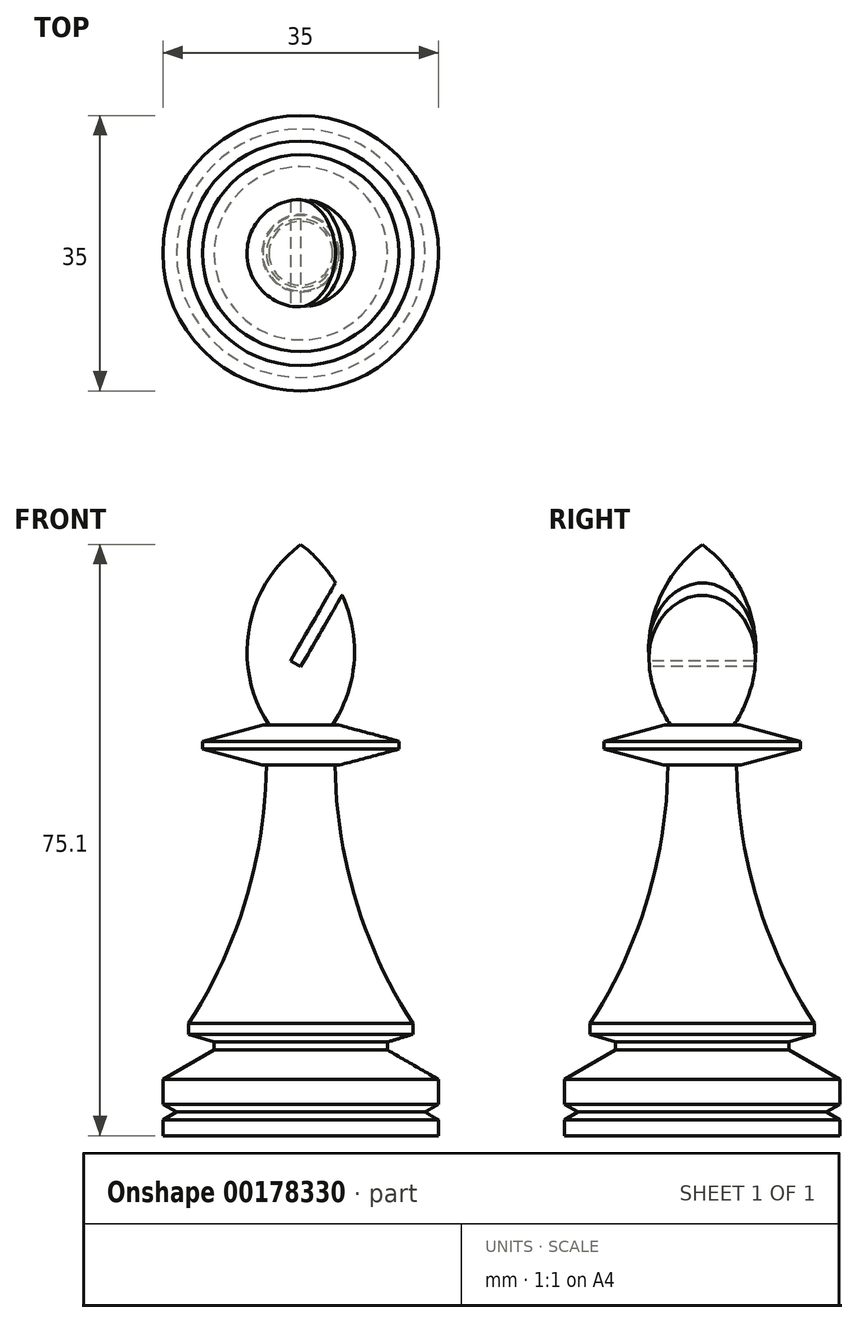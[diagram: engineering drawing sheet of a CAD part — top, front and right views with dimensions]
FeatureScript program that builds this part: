
annotation { "Feature Type Name" : "Feature", "Feature Type Description" : "" }
export const myFeature = defineFeature(function(context is Context, id is Id, definition is map)
    precondition{}
    {
        {
            var Q0;
            Q0=qCreatedBy(makeId("Front.planeOp"),FACE);
            var sketch = newSketch(context, id + "F0", { "sketchPlane" : qUnion([Q0])});
            skLineSegment(sketch, "E0", {"start": v(0, 0) * mm, "end": v(17.5, 0) * mm});
            skLineSegment(sketch, "E1", {"start": v(17.5, 0) * mm, "end": v(17.5, 2) * mm});
            skLineSegment(sketch, "E2", {"start": v(17.5, 7.13) * mm, "end": v(11, 10.89) * mm});
            skLineSegment(sketch, "E3", {"start": v(0, 14.4) * mm, "end": v(0, 0) * mm});
            skPoint(sketch, "E4.endSnap0", {"position": v(17.5, 3.57) * mm});
            skLineSegment(sketch, "E5", {"start": v(17.5, 2) * mm, "end": v(15.77, 3) * mm});
            skLineSegment(sketch, "E6", {"start": v(15.77, 3) * mm, "end": v(17.5, 4) * mm});
            skLineSegment(sketch, "E7.trimOffspring", {"start": v(17.5, 3.57) * mm, "end": v(17.5, 7.13) * mm});
            skLineSegment(sketch, "E8", {"start": v(11, 10.89) * mm, "end": v(11, 11.89) * mm});
            skLineSegment(sketch, "E9", {"start": v(11, 11.89) * mm, "end": v(14.25, 12.89) * mm});
            skLineSegment(sketch, "E10", {"start": v(14.25, 14.25) * mm, "end": v(14.25, 12.89) * mm});
            skLineSegment(sketch, "E11", {"start": v(0, 0) * mm, "end": v(0, 78) * mm});
            skArc(sketch, "E12", {"start": v(2.57, 74.16) * mm, "mid": v(1.37, 74.86) * mm, "end": v(0, 75.1) * mm});
            skPoint(sketch, "E13.first.point", {"position": v(2.57, 74.16) * mm});
            skPoint(sketch, "E13.third.point", {"position": v(10.83, 51.5) * mm});
            skLineSegment(sketch, "E14", {"start": v(12.5, 50.1) * mm, "end": v(12.5, 49.1) * mm});
            skLineSegment(sketch, "E15", {"start": v(12.5, 50.1) * mm, "end": v(4.8, 52.17) * mm});
            skLineSegment(sketch, "E16", {"start": v(12.5, 49.1) * mm, "end": v(4.92, 47.08) * mm});
            skLineSegment(sketch, "E17", {"start": v(4.05, 52.17) * mm, "end": v(4.8, 52.17) * mm});
            skArc(sketch, "E18", {"start": v(4.36, 47.09) * mm, "mid": v(6.97, 29.97) * mm, "end": v(14.25, 14.25) * mm});
            skPoint(sketch, "E18.first.point", {"position": v(4.36, 47.09) * mm});
            skPoint(sketch, "E18.second.point", {"position": v(75.46, -13.1) * mm});
            skPoint(sketch, "E18.third.point", {"position": v(14.25, 14.25) * mm});
            skPoint(sketch, "E19.orphan", {"position": v(0, 49.17) * mm});
            skPoint(sketch, "E20.start.orphan", {"position": v(0, 50.17) * mm});
            skLineSegment(sketch, "E21", {"start": v(0, 52.17) * mm, "end": v(0, 47.17) * mm});
            skLineSegment(sketch, "E22", {"start": v(4.92, 47.08) * mm, "end": v(4.36, 47.09) * mm});
            skArc(sketch, "E23", {"start": v(4.05, 52.17) * mm, "mid": v(6.57, 64.44) * mm, "end": v(0, 75.1) * mm});
            skPoint(sketch, "E23.second.point", {"position": v(-21.42, 48.8) * mm});
            skPoint(sketch, "E23.third.point", {"position": v(6.42, 65.18) * mm});
            skLineSegment(sketch, "E24", {"start": v(0, 75.1) * mm, "end": v(0, 0) * mm});
            skSolve(sketch);
        }
        {
            var Q0;
            {var subQ1=sQuery(id+"F0.wireOp",EDGE,"E0");Q0=makeQuery(id+"F0.imprint","IMPRINT",FACE,{"disambiguationData":[TD([[makeQuery(id+"F0.imprint","IMPRINT",EDGE,{"derivedFrom":subQ1}),1.0]])]});}
            var Q1;
            Q1=sQuery(id+"F0.wireOp",EDGE,"E3");
            revolve(context, id + "F1", {"entities" : qUnion([Q0]), "axis" : qUnion([Q1]), "revolveType" : RevolveType.FULL});
        }
        {
            var Q0;
            Q0=qCreatedBy(makeId("Front.planeOp"),FACE);
            var sketch = newSketch(context, id + "F2", { "sketchPlane" : qUnion([Q0])});
            skLineSegment(sketch, "E25", {"start": v(7.78, 73.05) * mm, "end": v(0, 59.58) * mm});
            skLineSegment(sketch, "E26", {"start": v(-25.93, 14.66) * mm, "end": v(-25.93, 70.38) * mm});
            skLineSegment(sketch, "E27.0", {"start": v(6.56, 73.94) * mm, "end": v(-1.3, 60.33) * mm});
            skLineSegment(sketch, "E28", {"start": v(0, 59.58) * mm, "end": v(-1.3, 60.33) * mm});
            skLineSegment(sketch, "E29", {"start": v(6.56, 73.94) * mm, "end": v(7.78, 73.05) * mm});
            skLineSegment(sketch, "E30", {"start": v(0, 59.58) * mm, "end": v(7.78, 73.05) * mm});
            skLineSegment(sketch, "E31", {"start": v(-1.3, 60.33) * mm, "end": v(6.56, 73.94) * mm});
            skLineSegment(sketch, "E32", {"start": v(-1.3, 60.33) * mm, "end": v(3.65, 68.9) * mm});
            skSolve(sketch);
        }
        {
            var Q0;
            Q0 = qSketchRegion(id + "F2", true);
            extrude(context, id + "F3", {"entities" : qUnion([Q0]), "operationType" : NewBodyOperationType.REMOVE, "oppositeDirection" : true, "depth" : 50 * mm, "offsetDistance" : 25 * mm, "symmetric" : true});
        }
    });
